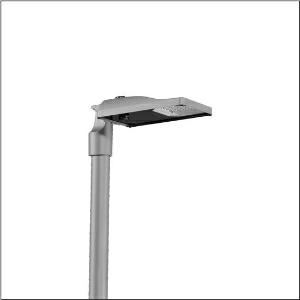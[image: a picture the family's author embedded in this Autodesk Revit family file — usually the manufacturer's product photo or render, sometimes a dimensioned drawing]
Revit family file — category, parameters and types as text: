
# Revit family: streetlight_sl_31_micro___st1_0a_5xh1d71t08da_c755
name_source: partatom
category: Lighting Fixtures
units: mm (PartAtom-declared; Revit-internal decimal feet)

## family parameters
Cut with Voids When Loaded = No
Host = Face
Light Source = No
Part Type = Normal
Room Calculation Point = No
Round Connector Dimension = Use Diameter
Shared = No

## types (1)
- --- (1 x LED, 3990 lm, 37.7 W, 2200K)
    Apparent Load = 38 VA
    CIE Flux Codes = 37 72 97 100 100
    Color Rendering = 70
    Color Temperature = 2200K
    Default Elevation = 1800 mm
    Description = Streetlight SL 31 micro D4i, Desk-Remote mast luminaire for post-top, side-entry; light control with lens of PMMA; light distribution: ST1.0a, direct asymmetric distribution, for standard-compliant lighting for roads and squares; LED: luminous flux: 3.990lm, light colour: 722, colour temperature: 2200K; luminous efficacy: 105,8lm/W; control: pre-setting: logarithmic dimming characteristic, flexible luminous flux parameterisation, time-dependent luminous flux control, constant luminous flux control, power reduction, intelligent temperature release in ECG and LED module, overheat protection; luminaire housing, of diecast aluminium, SITECO metallic grey (DB 702S), corrosivity category C5 high according to DIN EN ISO 12944; cover of toughened safety glass, transparent, mast flange of diecast aluminium, SITECO metallic grey (DB 702S), spigot size: 76/60mm, mast flange included unmounted; cable length: 6,5m, connection cable pre-assembled; mains connection: 220..240V, AC, 50/60Hz; power consumption (at start of service life): 37,7W / (at end of service life): 40,9W / (with reduced operation 50%): 16,3W; protection rating (complete): IP66; insulation class (complete): insulation class II (safety insulation); impact resistance: IK09; certification: CE, ENEC, ENEC+, VDE, UKCA, ZD4i; permissible operating ambient temperature for outdoor applications: -40..+50°C; packaging unit: 1 piece

Light Distribution: ST1.0a
    Height = 76 mm
    Lamp = 1 x LED
    Lamp Light Flux = 3990 lm
    Lamp Power = 37.7 W
    Lamp count = 1
    Length = 467 mm
    Luminous efficacy = 106 lm/W
    Manufacturer = Siteco
    ModVariant = No
    Model = 5XH1D71T08DA
    Mounting Place = Pole
    Mounting Type = Pole top
    Number of Poles = 1
    OnlyDefault = Yes
    Power Factor = 1
    Product Name = Streetlight SL 31 micro | ST1.0a
    Product group = mast luminaire | pylon top
    ProductGroupID = 6100
    Protection Class = Protection class II
    Protection Degree = IP 66
    RLX_Detail_Level = 1
    RLX_Emergency_Light_Flux = 0 lm
    RLX_Emergency_Type = 0
    RLX_Emergency_Type_DB = No
    RlxData = <blob elided: 23373 chars, md5=3ca94182>
    Socket = socket
    Standby Power = 0 W
    System Light Flux = 3990 lm
    System Power = 38 W
    Type Comments = factory setting: luminous flux: 100 % | dim-lin: 254 | 745 mA
    Type Image = l_1300315.jpg
    URL = http://relux.com
    VarID = @adj_011077
    Voltage = 0 V
    Weight = 0.00 kg
    Width = 265 mm

## geometry (parser evidence)
native form markers: Blend x4, Sweep x9
no freeform markers — native parametric forms only
